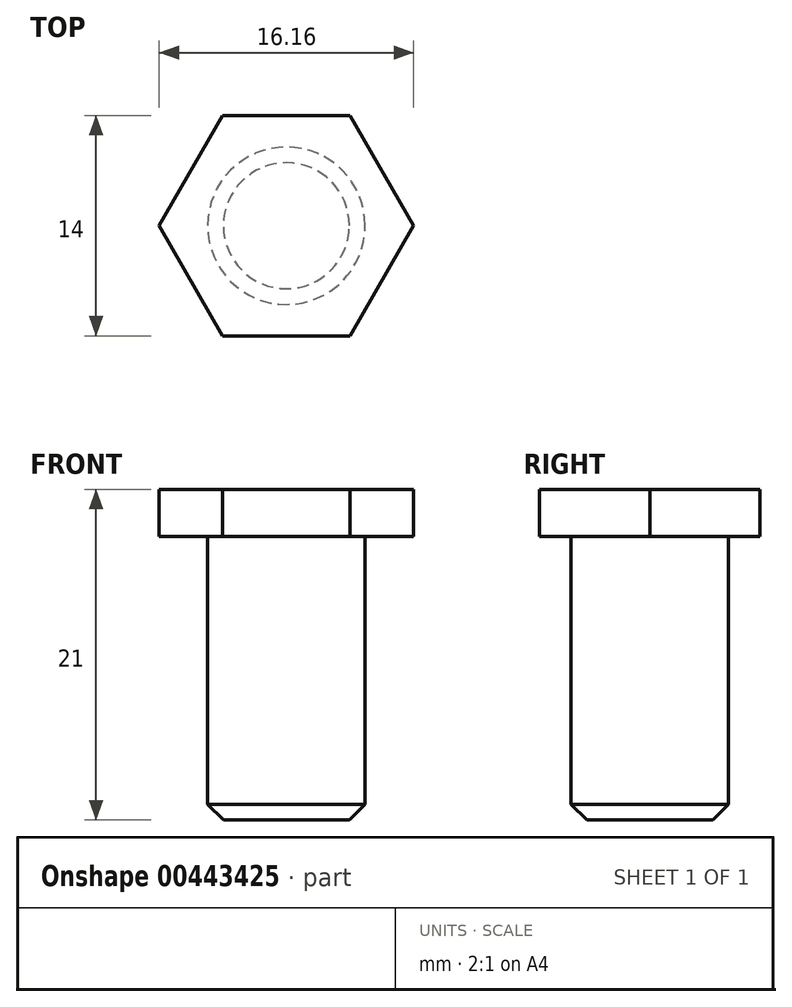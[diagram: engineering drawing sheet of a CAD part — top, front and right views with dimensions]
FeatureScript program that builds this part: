
annotation { "Feature Type Name" : "Feature", "Feature Type Description" : "" }
export const myFeature = defineFeature(function(context is Context, id is Id, definition is map)
    precondition{}
    {
        {
            var Q0;
            Q0=qCreatedBy(makeId("Top.planeOp"),FACE);
            var sketch = newSketch(context, id + "F0", { "sketchPlane" : qUnion([Q0])});
            skCircle(sketch, "E0", {"center": v(0, 0) * mm, "radius": 5 * mm});
            skSolve(sketch);
        }
        {
            var Q0;
            Q0=makeQuery(id+"F0.imprint","IMPRINT",FACE,{"disambiguationData":[TD([[makeQuery(id+"F0.imprint","IMPRINT",EDGE,{"derivedFrom":sQuery(id+"F0.wireOp",EDGE,"E0")}),1.0]])]});
            extrude(context, id + "F1", {"entities" : qUnion([Q0]), "depth" : 18 * mm});
        }
        {
            var Q0;
            Q0=makeQuery(id+"F1.opExtrude","CAP_EDGE",EDGE,{"disambiguationData":[OSD([sQuery(id+"F0.wireOp",EDGE,"E0")])],"isStart":true});
            chamfer(context, id + "F2", {"entities" : qUnion([Q0]), "chamferType" : ChamferType.OFFSET_ANGLE, "width" : 1 * mm, "oppositeDirection" : false, "angle" : 45 * degree, "tangentPropagation" : true});
        }
        {
            var Q0;
            Q0=makeQuery(id+"F1.opExtrude","CAP_FACE",FACE,{"disambiguationData":[OSD([sQuery(id+"F0.wireOp",EDGE,"E0")])],"isStart":false});
            var sketch = newSketch(context, id + "F3", { "sketchPlane" : qUnion([Q0])});
            skCircle(sketch, "E1.cCircle", {"center": v(0, 0) * mm, "radius": 7 * mm, "construction": true});
            skLineSegment(sketch, "E1.0", {"start": v(4.04, 7) * mm, "end": v(8.08, 0) * mm});
            skLineSegment(sketch, "E1.1", {"start": v(8.08, 0) * mm, "end": v(4.04, -7) * mm});
            skLineSegment(sketch, "E1.2", {"start": v(4.04, -7) * mm, "end": v(-4.04, -7) * mm});
            skLineSegment(sketch, "E1.3", {"start": v(-4.04, -7) * mm, "end": v(-8.08, 0) * mm});
            skLineSegment(sketch, "E1.4", {"start": v(-8.08, 0) * mm, "end": v(-4.04, 7) * mm});
            skLineSegment(sketch, "E1.5", {"start": v(-4.04, 7) * mm, "end": v(4.04, 7) * mm});
            skPoint(sketch, "E1.0.midPoint", {"position": v(6.06, 3.5) * mm});
            skSolve(sketch);
        }
        {
            var Q0;
            Q0 = qSketchRegion(id + "F3", true);
            extrude(context, id + "F4", {"entities" : qUnion([Q0]), "operationType" : NewBodyOperationType.ADD, "depth" : 3 * mm});
        }
    });
